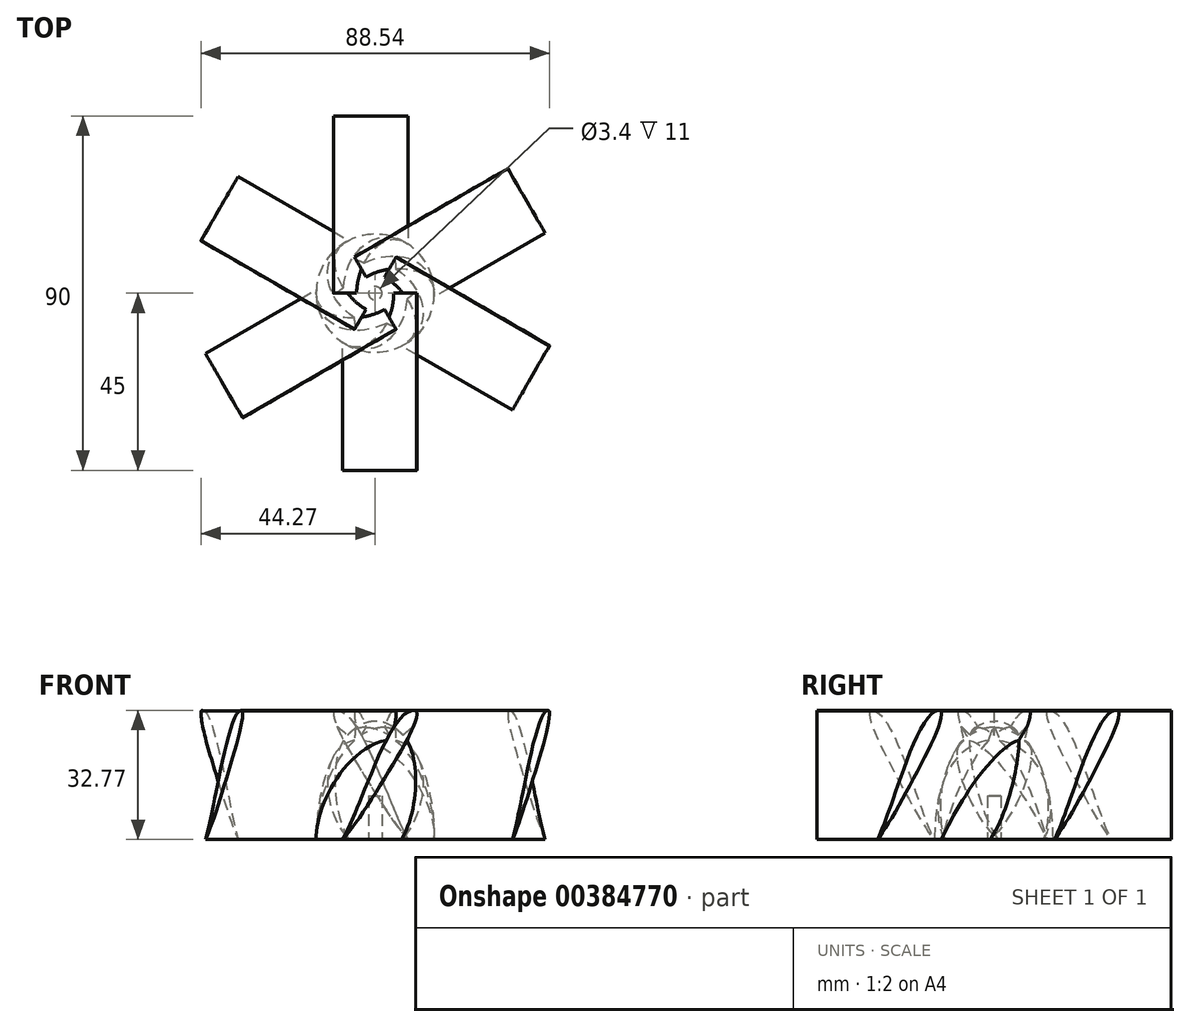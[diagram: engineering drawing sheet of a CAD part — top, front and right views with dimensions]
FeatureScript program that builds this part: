
annotation { "Feature Type Name" : "Feature", "Feature Type Description" : "" }
export const myFeature = defineFeature(function(context is Context, id is Id, definition is map)
    precondition{}
    {
        {
            assignVariable(context, id + "F0", {"name" : "impeller_diameter", "anyValue" : 30});
        }
        {
            assignVariable(context, id + "F1", {"name" : "number_of_blades", "anyValue" : 6});
        }
        {
            assignVariable(context, id + "F2", {"name" : "hole_height", "anyValue" : 11});
        }
        {
            assignVariable(context, id + "F3", {"name" : "blade_lenght", "anyValue" : getVariable(context, 'impeller_diameter') * 1.5});
        }
        {
            var Q0;
            Q0=qCreatedBy(makeId("Front.planeOp"),FACE);
            var sketch = newSketch(context, id + "F4", { "sketchPlane" : qUnion([Q0])});
            skEllipticalArc(sketch, "E0", {});
            skLineSegment(sketch, "E1", {"start": v(-15, 0) * mm, "end": v(15, 0) * mm});
            skLineSegment(sketch, "E2", {"start": v(0, 0) * mm, "end": v(0, 50) * mm});
            const initialGuessF4  = {"E0": [0, 0, 0, 1, 0.03, 0.015, 4.71238898038469, 1.5707963267948966]};
            skSetInitialGuess(sketch, initialGuessF4);
            skSolve(sketch);
        }
        {
            var Q0;
            {var subQ0=sQuery(id+"F4.wireOp",EDGE,"E2");Q0=makeQuery(id+"F4.imprint","IMPRINT",FACE,{"disambiguationData":[TD([[makeQuery(id+"F4.imprint","IMPRINT",EDGE,{"derivedFrom":subQ0}),1.0]])]});}
            var Q1;
            Q1=sQuery(id+"F4.wireOp",EDGE,"E2");
            revolve(context, id + "F5", {"entities" : qUnion([Q0]), "axis" : qUnion([Q1]), "revolveType" : RevolveType.FULL});
        }
        {
            var Q0;
            Q0=qCreatedBy(makeId("Front.planeOp"),FACE);
            var sketch = newSketch(context, id + "F6", { "sketchPlane" : qUnion([Q0])});
            skLineSegment(sketch, "E3", {"start": v(-10, 0) * mm, "end": v(9.25, 33.33) * mm, "construction": true});
            skLineSegment(sketch, "E4", {"start": v(9.25, 33.33) * mm, "end": v(11.84, 31.83) * mm, "construction": true});
            skLineSegment(sketch, "E5", {"start": v(11.84, 31.83) * mm, "end": v(-6.54, 0) * mm, "construction": true});
            skLineSegment(sketch, "E6", {"start": v(-6.54, 0) * mm, "end": v(-10, 0) * mm});
            skFitSpline(sketch, "E7", {"points": [v(10.54, 32.58) * mm, v(-2.71, 12.62) * mm, v(-8.27, 0) * mm], "startDerivative": vector(-23.59, 10.36) * mm, "endDerivative": vector(-13.36, -25.44) * mm});
            skFitSpline(sketch, "E8", {"points": [v(10.54, 32.58) * mm, v(3.75, 17.8) * mm, v(-8.27, 0) * mm], "startDerivative": vector(3.34, -16.17) * mm, "endDerivative": vector(-15.35, -15.95) * mm});
            skSolve(sketch);
        }
        {
            var Q0;
            Q0=qSketchRegion(id+"F6",true);
            extrude(context, id + "F7", {"entities" : qUnion([Q0]), "operationType" : NewBodyOperationType.ADD, "depth" : (getVariable(context, 'blade_lenght')) * mm});
        }
        {
            var Q0;
            Q0=makeQuery(id+"F5.opRevolve","SWEPT_BODY",BODY,{"disambiguationData":[OSD([sQuery(id+"F4.wireOp",EDGE,"E0"),sQuery(id+"F4.wireOp",EDGE,"E1"),sQuery(id+"F4.wireOp",EDGE,"E2")])]});
            var Q1;
            Q1=makeQuery(id+"F5.opRevolve","SWEPT_EDGE",EDGE,{"disambiguationData":[OSD([sQuery(id+"F4.wireOp",EDGE,"E0"),sQuery(id+"F4.wireOp",EDGE,"E1")])]});
            circularPattern(context, id + "F8", {"operationType" : NewBodyOperationType.ADD, "entities" : qUnion([Q0]), "axis" : qUnion([Q1]), "angle" : 360 * degree, "instanceCount" : getVariable(context, 'number_of_blades'), "equalSpace" : true});
        }
        {
            var Q0;
            Q0=makeQuery(id+"F5.opRevolve","SWEPT_FACE",FACE,{"disambiguationData":[OSD([sQuery(id+"F4.wireOp",EDGE,"E1")])]});
            var sketch = newSketch(context, id + "F9", { "sketchPlane" : qUnion([Q0])});
            skCircle(sketch, "E9", {"center": v(0, 0) * mm, "radius": 1.7 * mm});
            skSolve(sketch);
        }
        {
            var Q0;
            Q0=makeQuery(id+"F9.imprint","IMPRINT",FACE,{"disambiguationData":[TD([[makeQuery(id+"F9.imprint","IMPRINT",EDGE,{"derivedFrom":sQuery(id+"F9.wireOp",EDGE,"E9")}),1.0]])]});
            extrude(context, id + "F10", {"entities" : qUnion([Q0]), "operationType" : NewBodyOperationType.REMOVE, "oppositeDirection" : true, "depth" : (getVariable(context, 'hole_height')) * mm});
        }
    });
